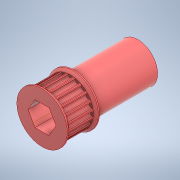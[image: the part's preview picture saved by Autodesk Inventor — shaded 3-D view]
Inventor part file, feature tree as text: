
AUTODESK INVENTOR PART (.ipt)
format: ipt  version: 2022.3 (Build 263350000, 350)  size: 297,472 bytes
history: native  units: in
note: dims shown in document units (in); Inventor stores cm internally (conversion verified against a paired STEP export)
features: extrude x7, sketch x7, mirror x2, chamfer x2, other x1, fillet x1, pattern_circular x1, projected_geometry x1
ambient origin geometry x8: Origin, YZ Plane, XZ Plane, XY Plane, X Axis, Y Axis, Z Axis, Center Point
bodies: Solid1 (feature_tree)
feature tree (22):
  other  "Hex Bore"
  extrude  "HTD Base"  Depth=0.3937in TaperAngle=0.0deg
  extrude  "HTD Flange"  Depth=0.0591in
  mirror  "HTD Flanges"
  chamfer  "HTD Flange Chamfer"  Distance=0.0787in Angle=45.0deg
  extrude  "GT2 Base"  TaperAngle=0.0deg  [1 undecoded]
  extrude  "GT2 Base Tooth"  TaperAngle=0.0deg  [1 undecoded]
  fillet  "GT2 Base Tooth pt. 2"  Radius=0.7219in
  pattern_circular  "GT2 Teeth"  [2 undecoded]
  extrude  "GT2 Flange"  Depth=1.01in
  mirror  "GT2 Flanges"
  chamfer  "GT2 Flange Chamfer"  Distance=0.0075in
  extrude  "Circle Bore"  TaperAngle=0.0deg  [1 undecoded]
  extrude  "Extrusion9"  Depth=0.0118in
  sketch  "Sketch1"  dims[d0=1.2082in d1=0.3937in d2=0.0in]
  sketch  "Sketch4"  dims[d12=0.0394in d13=0.0591in]
  sketch  "Sketch5"  dims[d14=0.0in]
  sketch  "Sketch6"  dims[d15=0.0394in d16=0.0787in d17=45.0deg]
  sketch  "Sketch7"  dims[d18=0.385in d19=0.0in d20=0.0in]
  sketch  "Sketch8"  dims[d21=0.385in d22=0.0in d23=0.0in d24=0.7219in]
  sketch  "Sketch9"  dims[d25=0.3937in d26=0.0in d27=0.0727in d28=0.0075in d29=0.0in d30=0.0in d31=0.0118in d32=7.874in d33=360.0deg d35=0.0394in d36=0.0591in d37=0.0in d38=0.0394in d39=0.0787in d40=45.0deg d41=0.625in d42=1.01in d43=0.0in]
  projected_geometry  "Projected Loop1"
note: 5 required parameter values undecoded (feature->parameter linkage not recoverable at this tier; creation-order binding heuristic only, values carry confidence <= 0.55)
